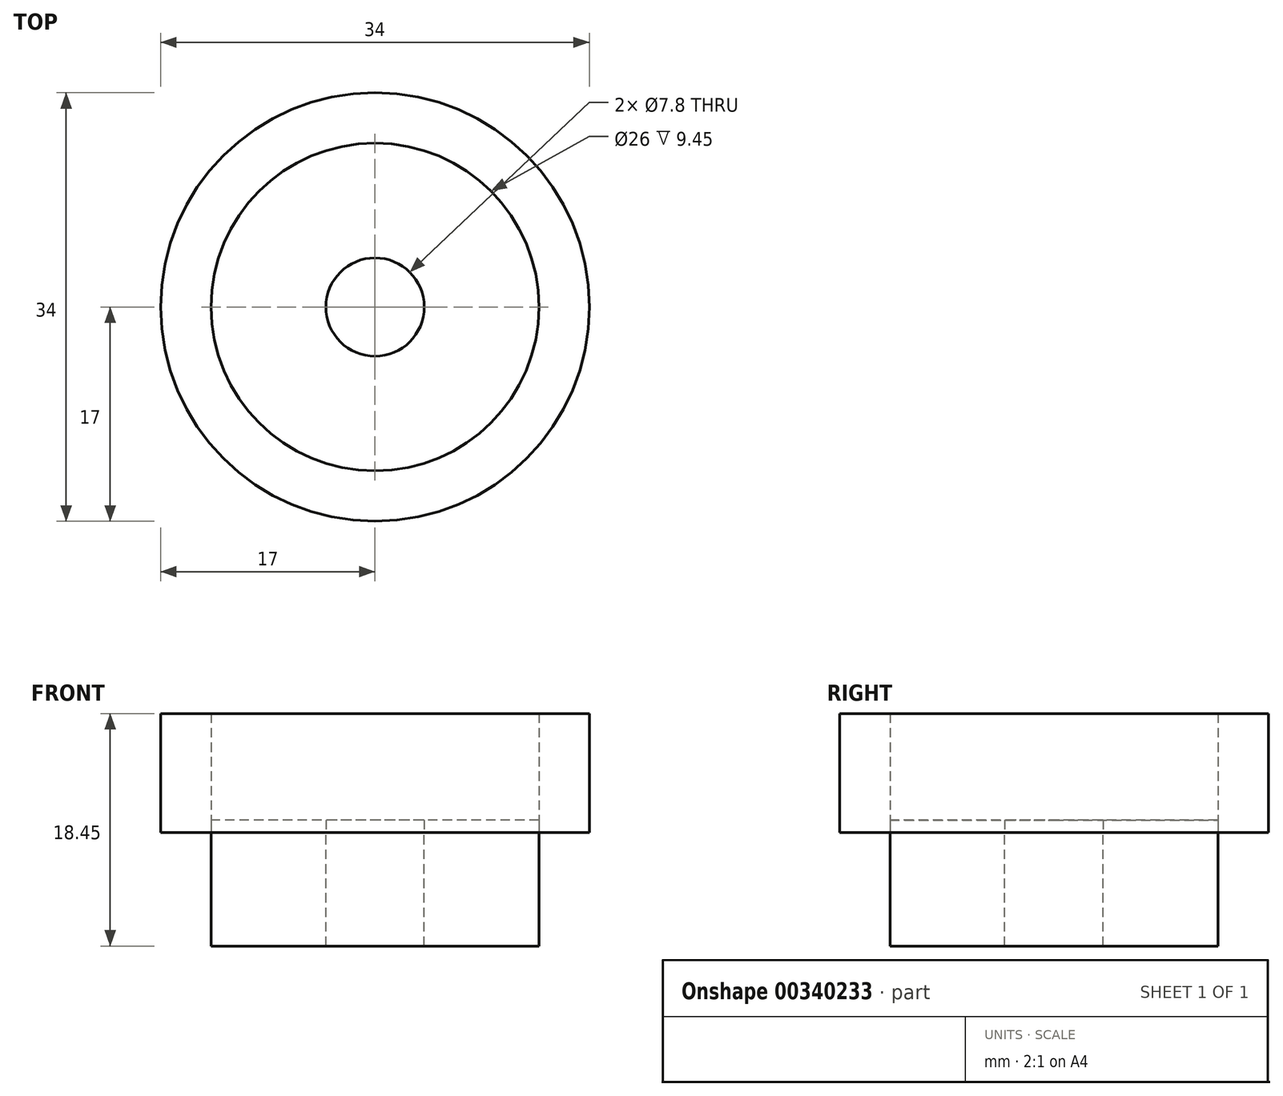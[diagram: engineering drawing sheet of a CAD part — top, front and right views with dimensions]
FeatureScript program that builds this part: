
annotation { "Feature Type Name" : "Feature", "Feature Type Description" : "" }
export const myFeature = defineFeature(function(context is Context, id is Id, definition is map)
    precondition{}
    {
        {
            var Q0;
            Q0=qCreatedBy(makeId("Top.planeOp"),FACE);
            var sketch = newSketch(context, id + "F0", { "sketchPlane" : qUnion([Q0])});
            skCircle(sketch, "E0", {"center": v(0, 0) * mm, "radius": 13 * mm});
            skCircle(sketch, "E1", {"center": v(0, 0) * mm, "radius": 3.9 * mm});
            skCircle(sketch, "E2", {"center": v(0, 0) * mm, "radius": 17 * mm});
            skSolve(sketch);
        }
        {
            var Q0;
            Q0=makeQuery(id+"F0.imprint","IMPRINT",FACE,{"disambiguationData":[TD([[makeQuery(id+"F0.imprint","IMPRINT",EDGE,{"derivedFrom":sQuery(id+"F0.wireOp",EDGE,"E0")}),1.0]])]});
            extrude(context, id + "F1", {"entities" : qUnion([Q0]), "oppositeDirection" : true, "depth" : 9 * mm});
        }
        {
            var Q0;
            Q0=makeQuery(id+"F0.imprint","IMPRINT",FACE,{"disambiguationData":[TD([[makeQuery(id+"F0.imprint","IMPRINT",EDGE,{"derivedFrom":sQuery(id+"F0.wireOp",EDGE,"E0")}),-1.0]])]});
            extrude(context, id + "F2", {"entities" : qUnion([Q0]), "depth" : 9.45 * mm});
        }
        {
            var Q0;
            Q0=makeQuery(id+"F0.imprint","IMPRINT",FACE,{"disambiguationData":[TD([[makeQuery(id+"F0.imprint","IMPRINT",EDGE,{"derivedFrom":sQuery(id+"F0.wireOp",EDGE,"E0")}),1.0]])]});
            extrude(context, id + "F3", {"entities" : qUnion([Q0]), "depth" : 1 * mm});
        }
    });
